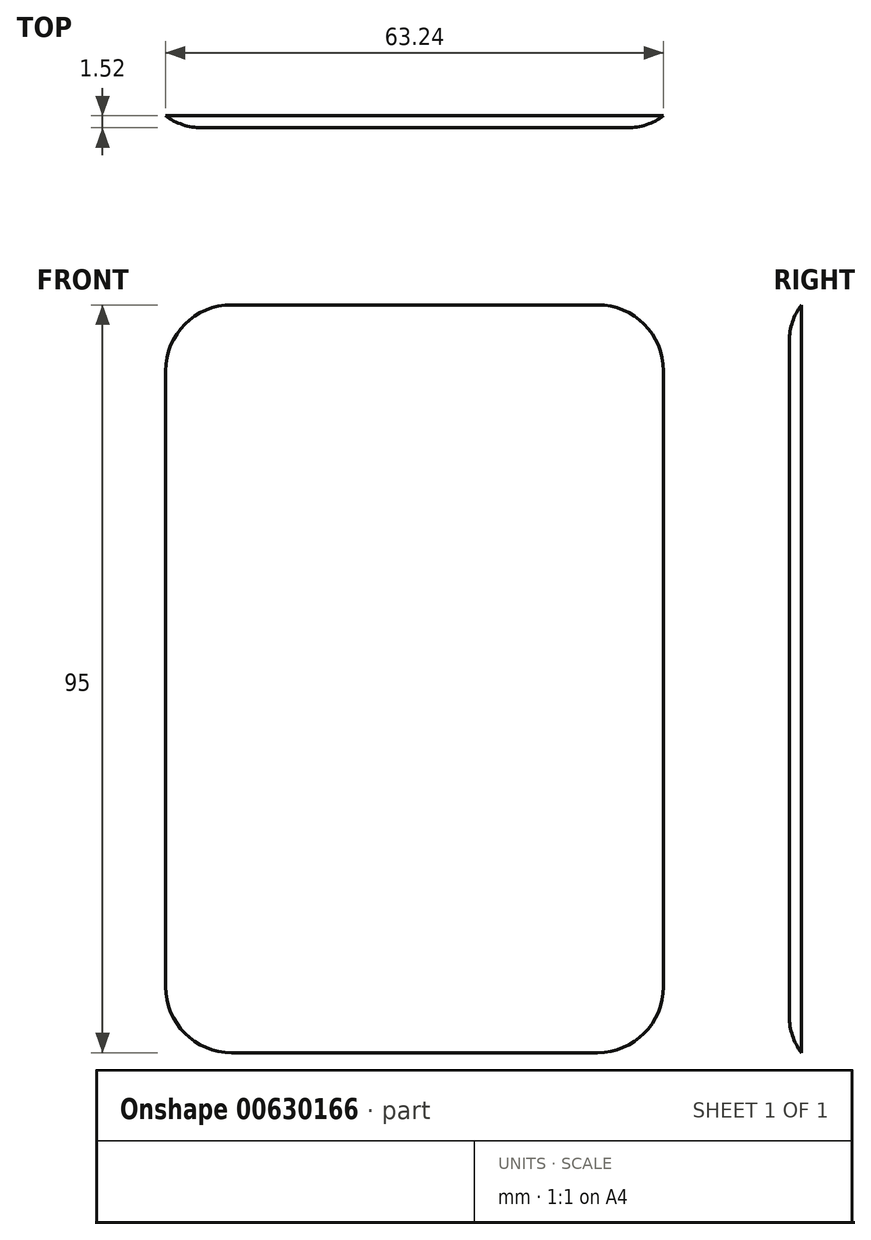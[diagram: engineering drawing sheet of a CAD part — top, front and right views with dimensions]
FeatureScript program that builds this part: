
annotation { "Feature Type Name" : "Feature", "Feature Type Description" : "" }
export const myFeature = defineFeature(function(context is Context, id is Id, definition is map)
    precondition{}
    {
        {
            var Q0;
            Q0=qCreatedBy(makeId("Front.planeOp"),FACE);
            var sketch = newSketch(context, id + "F0", { "sketchPlane" : qUnion([Q0])});
            skLineSegment(sketch, "E0.bottom", {"start": v(23.24, -47.5) * mm, "end": v(-23.24, -47.5) * mm});
            skLineSegment(sketch, "E0.top", {"start": v(23.24, 47.5) * mm, "end": v(-23.24, 47.5) * mm});
            skLineSegment(sketch, "E0.left", {"start": v(31.62, -39.12) * mm, "end": v(31.62, 39.12) * mm});
            skLineSegment(sketch, "E0.right", {"start": v(-31.62, -39.12) * mm, "end": v(-31.62, 39.12) * mm});
            skPoint(sketch, "E0.middle", {"position": v(0, 0) * mm});
            skPoint(sketch, "E1.visualSharp", {"position": v(-31.62, 47.5) * mm});
            skArc(sketch, "E1.filletArc", {"start": v(-23.24, 47.5) * mm, "mid": v(-29.17, 45.04) * mm, "end": v(-31.62, 39.12) * mm});
            skPoint(sketch, "E2.visualSharp", {"position": v(31.62, -47.5) * mm});
            skArc(sketch, "E2.filletArc", {"start": v(23.24, -47.5) * mm, "mid": v(29.17, -45.04) * mm, "end": v(31.62, -39.12) * mm});
            skPoint(sketch, "E3.visualSharp", {"position": v(-31.62, -47.5) * mm});
            skArc(sketch, "E3.filletArc", {"start": v(-31.62, -39.12) * mm, "mid": v(-29.17, -45.04) * mm, "end": v(-23.24, -47.5) * mm});
            skPoint(sketch, "E4.visualSharp", {"position": v(31.62, 47.5) * mm});
            skArc(sketch, "E4.filletArc", {"start": v(31.62, 39.12) * mm, "mid": v(29.17, 45.04) * mm, "end": v(23.24, 47.5) * mm});
            skSolve(sketch);
        }
        {
            var Q0;
            Q0 = qSketchRegion(id + "F0", true);
            extrude(context, id + "F1", {"entities" : qUnion([Q0]), "depth" : 1.52 * mm, "offsetDistance" : 25.4 * mm});
        }
        {
            var Q0;
            Q0=makeQuery(id+"F1.opExtrude","CAP_EDGE",EDGE,{"disambiguationData":[OSD([sQuery(id+"F0.wireOp",EDGE,"E0.right")])],"isStart":false});
            fillet(context, id + "F2", {"entities" : qUnion([Q0]), "radius" : 7.62 * mm, "tangentPropagation" : true, "allowEdgeOverflow" : false});
        }
    });
